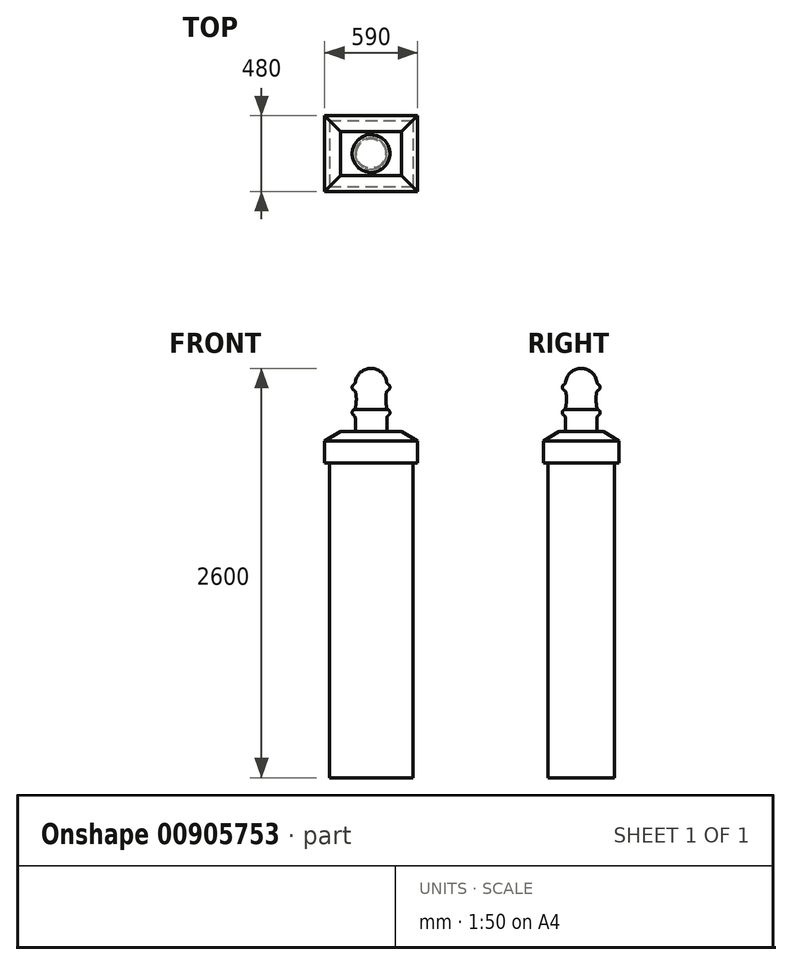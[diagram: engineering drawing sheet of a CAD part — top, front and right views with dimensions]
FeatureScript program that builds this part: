
annotation { "Feature Type Name" : "Feature", "Feature Type Description" : "" }
export const myFeature = defineFeature(function(context is Context, id is Id, definition is map)
    precondition{}
    {
        {
            var Q0;
            Q0=qCreatedBy(makeId("Top.planeOp"),FACE);
            var sketch = newSketch(context, id + "F0", { "sketchPlane" : qUnion([Q0])});
            skLineSegment(sketch, "E0.bottom", {"start": v(-265, 210) * mm, "end": v(265, 210) * mm});
            skLineSegment(sketch, "E0.top", {"start": v(-265, -210) * mm, "end": v(265, -210) * mm});
            skLineSegment(sketch, "E0.left", {"start": v(-265, 210) * mm, "end": v(-265, -210) * mm});
            skLineSegment(sketch, "E0.right", {"start": v(265, 210) * mm, "end": v(265, -210) * mm});
            skSolve(sketch);
        }
        {
            var Q0;
            Q0=qSketchRegion(id+"F0",true);
            extrude(context, id + "F1", {"entities" : qUnion([Q0]), "depth" : 2000 * mm, "offsetDistance" : 25.4 * mm});
        }
        {
            var Q0;
            Q0=makeQuery(id+"F1.opExtrude","CAP_FACE",FACE,{"disambiguationData":[OSD([sQuery(id+"F0.wireOp",EDGE,"E0.bottom"),sQuery(id+"F0.wireOp",EDGE,"E0.top"),sQuery(id+"F0.wireOp",EDGE,"E0.left"),sQuery(id+"F0.wireOp",EDGE,"E0.right")])],"isStart":false});
            var sketch = newSketch(context, id + "F2", { "sketchPlane" : qUnion([Q0])});
            skLineSegment(sketch, "E1.bottom", {"start": v(-295, 240) * mm, "end": v(295, 240) * mm});
            skLineSegment(sketch, "E1.top", {"start": v(-295, -240) * mm, "end": v(295, -240) * mm});
            skLineSegment(sketch, "E1.left", {"start": v(-295, 240) * mm, "end": v(-295, -240) * mm});
            skLineSegment(sketch, "E1.right", {"start": v(295, 240) * mm, "end": v(295, -240) * mm});
            skSolve(sketch);
        }
        {
            var Q0;
            Q0=qSketchRegion(id+"F2",true);
            extrude(context, id + "F3", {"entities" : qUnion([Q0]), "operationType" : NewBodyOperationType.ADD, "depth" : 100 * mm, "offsetDistance" : 25.4 * mm});
        }
        {
            var Q0;
            Q0=qCreatedBy(makeId("Right.planeOp"),FACE);
            var sketch = newSketch(context, id + "F4", { "sketchPlane" : qUnion([Q0])});
            skLineSegment(sketch, "E2.0", {"start": v(-240, 2100) * mm, "end": v(-240, 2000) * mm, "construction": true});
            skLineSegment(sketch, "E3.0", {"start": v(240, 2100) * mm, "end": v(-240, 2100) * mm, "construction": true});
            skLineSegment(sketch, "E4", {"start": v(-240, 2100) * mm, "end": v(-240, 2140) * mm});
            skLineSegment(sketch, "E5", {"start": v(-240, 2100) * mm, "end": v(-140, 2100) * mm});
            skLineSegment(sketch, "E6", {"start": v(-140, 2100) * mm, "end": v(-140, 2200) * mm});
            skLineSegment(sketch, "E7", {"start": v(-240, 2140) * mm, "end": v(-234.56, 2140) * mm, "construction": true});
            skLineSegment(sketch, "E8", {"start": v(-140, 2200) * mm, "end": v(-180, 2200) * mm, "construction": true});
            skLineSegment(sketch, "E9", {"start": v(-180, 2200) * mm, "end": v(-187.28, 2180) * mm, "construction": true});
            skLineSegment(sketch, "E10", {"start": v(-187.28, 2180) * mm, "end": v(-220, 2180) * mm, "construction": true});
            skLineSegment(sketch, "E11", {"start": v(-220, 2180) * mm, "end": v(-234.56, 2140) * mm, "construction": true});
            skLineSegment(sketch, "E12", {"start": v(-240, 2140) * mm, "end": v(-140, 2200) * mm});
            skSolve(sketch);
        }
        {
            var Q0;
            Q0=qSketchRegion(id+"F4",true);
            var Q1;
            Q1=makeQuery(id+"F3.opExtrude","CAP_EDGE",EDGE,{"disambiguationData":[OSD([sQuery(id+"F2.wireOp",EDGE,"E1.top")])],"isStart":false});
            var Q2;
            Q2=makeQuery(id+"F3.opExtrude","CAP_EDGE",EDGE,{"disambiguationData":[OSD([sQuery(id+"F2.wireOp",EDGE,"E1.right")])],"isStart":false});
            var Q3;
            Q3=makeQuery(id+"F3.opExtrude","CAP_EDGE",EDGE,{"disambiguationData":[OSD([sQuery(id+"F2.wireOp",EDGE,"E1.bottom")])],"isStart":false});
            var Q4;
            Q4=makeQuery(id+"F3.opExtrude","CAP_EDGE",EDGE,{"disambiguationData":[OSD([sQuery(id+"F2.wireOp",EDGE,"E1.left")])],"isStart":false});
            sweep(context, id + "F5", {"profiles" : qUnion([Q0]), "path" : qUnion([Q1, Q2, Q3, Q4])});
        }
        {
            var Q0;
            Q0=makeQuery(id+"F5.opSweep","SWEPT_FACE",FACE,{"disambiguationData":[OSD([sQuery(id+"F2.wireOp",EDGE,"E1.right"),sQuery(id+"F4.wireOp",EDGE,"E6")])]});
            var sketch = newSketch(context, id + "F6", { "sketchPlane" : qUnion([Q0])});
            skLineSegment(sketch, "E13.0", {"start": v(140, 2200) * mm, "end": v(140, 2100) * mm});
            skLineSegment(sketch, "E13.1", {"start": v(140, 2200) * mm, "end": v(-140, 2200) * mm});
            skLineSegment(sketch, "E13.2", {"start": v(140, 2100) * mm, "end": v(-140, 2100) * mm});
            skLineSegment(sketch, "E13.3", {"start": v(-140, 2200) * mm, "end": v(-140, 2100) * mm});
            skSolve(sketch);
        }
        {
            var Q0;
            Q0=qSketchRegion(id+"F6",true);
            var Q1;
            Q1=makeQuery(id+"F5.opSweep","SWEPT_FACE",FACE,{"disambiguationData":[OSD([sQuery(id+"F2.wireOp",EDGE,"E1.left"),sQuery(id+"F4.wireOp",EDGE,"E6")])]});
            var Q2;
            Q2=makeQuery(id+"F5.opSweep","MID_CAP_VERTEX",VERTEX,{"disambiguationData":[OSD([sQuery(id+"F2.wireOp",EDGE,"E1.bottom"),sQuery(id+"F4.wireOp",EDGE,"E5"),sQuery(id+"F4.wireOp",EDGE,"E6")])],"capPos":2.0});
            extrude(context, id + "F7", {"entities" : qUnion([Q0]), "operationType" : NewBodyOperationType.ADD, "endBound" : BoundingType.UP_TO_SURFACE, "depth" : 25.4 * mm, "endBoundEntityFace" : qUnion([Q1]), "endBoundEntityVertex" : qUnion([Q2]), "offsetDistance" : 25.4 * mm});
        }
        {
            var Q0;
            Q0=qCreatedBy(makeId("Right.planeOp"),FACE);
            var sketch = newSketch(context, id + "F8", { "sketchPlane" : qUnion([Q0])});
            skLineSegment(sketch, "E14", {"start": v(0, 0) * mm, "end": v(0, 2600) * mm, "construction": true});
            skLineSegment(sketch, "E15.0", {"start": v(-305, 2200) * mm, "end": v(305, 2200) * mm, "construction": true});
            skLineSegment(sketch, "E16", {"start": v(0, 2200) * mm, "end": v(100, 2200) * mm});
            skLineSegment(sketch, "E17", {"start": v(100, 2200) * mm, "end": v(100, 2300) * mm});
            skLineSegment(sketch, "E18", {"start": v(0, 2600) * mm, "end": v(0, 2200) * mm});
            skArc(sketch, "E19", {"start": v(100, 2500) * mm, "mid": v(70.71, 2570.71) * mm, "end": v(0, 2600) * mm});
            skArc(sketch, "E20", {"start": v(100, 2460) * mm, "mid": v(120, 2480) * mm, "end": v(100, 2500) * mm});
            skArc(sketch, "E21", {"start": v(100, 2460) * mm, "mid": v(93.77, 2404.55) * mm, "end": v(100, 2349.1) * mm});
            skArc(sketch, "E22", {"start": v(100, 2340) * mm, "mid": v(100.51, 2344.55) * mm, "end": v(100, 2349.1) * mm});
            skLineSegment(sketch, "E23", {"start": v(120, 2480) * mm, "end": v(120, 2655.72) * mm, "construction": true});
            skLineSegment(sketch, "E24", {"start": v(80, 2255.03) * mm, "end": v(80, 2460.6) * mm, "construction": true});
            skArc(sketch, "E25", {"start": v(100, 2300) * mm, "mid": v(120, 2320) * mm, "end": v(100, 2340) * mm});
            skSolve(sketch);
        }
        {
            var Q0;
            Q0=qSketchRegion(id+"F8",true);
            var Q1;
            Q1=sQuery(id+"F8.wireOp",EDGE,"E14");
            revolve(context, id + "F9", {"operationType" : NewBodyOperationType.ADD, "surfaceOperationType" : NewSurfaceOperationType.NEW, "entities" : qUnion([Q0]), "axis" : qUnion([Q1]), "revolveType" : RevolveType.FULL});
        }
        {
            var Q0;
            Q0=makeQuery(id+"F9.opRevolve","SWEPT_EDGE",EDGE,{"disambiguationData":[OSD([sQuery(id+"F8.wireOp",EDGE,"E17"),sQuery(id+"F8.wireOp",EDGE,"E25")])]});
            var Q1;
            Q1=makeQuery(id+"F9.opRevolve","SWEPT_EDGE",EDGE,{"disambiguationData":[OSD([sQuery(id+"F8.wireOp",EDGE,"E20"),sQuery(id+"F8.wireOp",EDGE,"E21")])]});
            var Q2;
            Q2=makeQuery(id+"F9.opRevolve","SWEPT_EDGE",EDGE,{"disambiguationData":[OSD([sQuery(id+"F8.wireOp",EDGE,"E19"),sQuery(id+"F8.wireOp",EDGE,"E20")])]});
            var Q3;
            Q3=makeQuery(id+"F9.opRevolve","SWEPT_EDGE",EDGE,{"disambiguationData":[OSD([sQuery(id+"F8.wireOp",EDGE,"E16"),sQuery(id+"F8.wireOp",EDGE,"E17")])]});
            fillet(context, id + "F10", {"entities" : qUnion([Q0, Q1, Q2, Q3]), "radius" : 25.4 * mm, "tangentPropagation" : true, "allowEdgeOverflow" : false});
        }
    });
